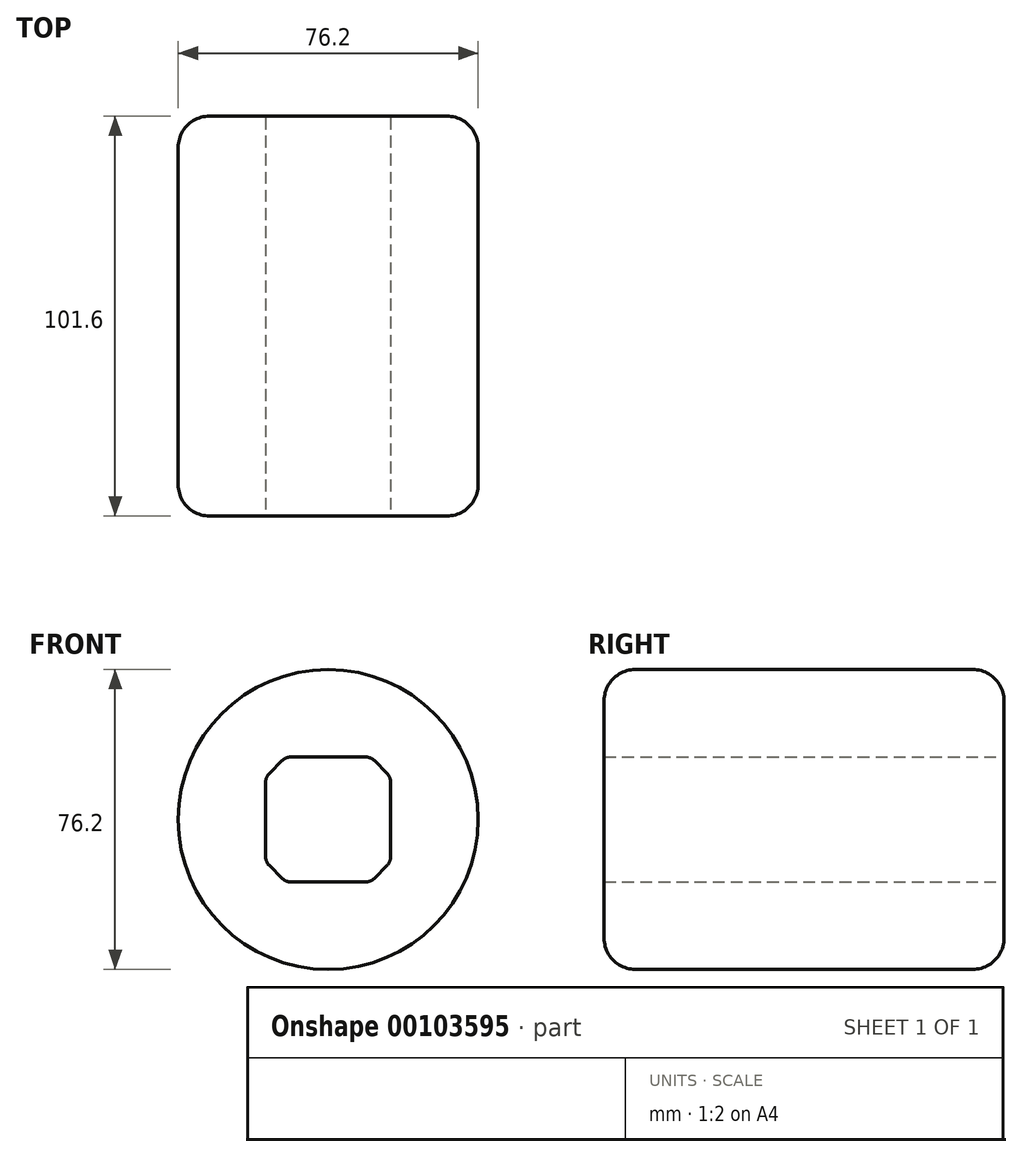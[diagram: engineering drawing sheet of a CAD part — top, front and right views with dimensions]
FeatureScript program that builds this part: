
annotation { "Feature Type Name" : "Feature", "Feature Type Description" : "" }
export const myFeature = defineFeature(function(context is Context, id is Id, definition is map)
    precondition{}
    {
        {
            var Q0;
            Q0=qCreatedBy(makeId("Front.planeOp"),FACE);
            var sketch = newSketch(context, id + "F0", { "sketchPlane" : qUnion([Q0])});
            skCircle(sketch, "E0", {"center": v(0, 0) * mm, "radius": 38.1 * mm});
            skSolve(sketch);
        }
        {
            var Q0;
            Q0 = qSketchRegion(id + "F0", true);
            extrude(context, id + "F1", {"entities" : qUnion([Q0]), "endBound" : BoundingType.SYMMETRIC, "depth" : 101.6 * mm});
        }
        {
            var Q0;
            Q0=makeQuery(id+"F1.opExtrude","CAP_EDGE",EDGE,{"disambiguationData":[OSD([sQuery(id+"F0.wireOp",EDGE,"E0")])],"isStart":false});
            var Q1;
            Q1=makeQuery(id+"F1.opExtrude","CAP_EDGE",EDGE,{"disambiguationData":[OSD([sQuery(id+"F0.wireOp",EDGE,"E0")])],"isStart":true});
            fillet(context, id + "F2", {"entities" : qUnion([Q0, Q1]), "radius" : 7.94 * mm, "tangentPropagation" : true, "allowEdgeOverflow" : false});
        }
        {
            var Q0;
            Q0=makeQuery(id+"F1.opExtrude","CAP_FACE",FACE,{"disambiguationData":[OSD([sQuery(id+"F0.wireOp",EDGE,"E0")])],"isStart":false});
            var sketch = newSketch(context, id + "F3", { "sketchPlane" : qUnion([Q0])});
            skLineSegment(sketch, "E1.bottom", {"start": v(15.88, -15.87) * mm, "end": v(-15.88, -15.88) * mm});
            skLineSegment(sketch, "E1.top", {"start": v(15.88, 15.88) * mm, "end": v(-15.88, 15.87) * mm});
            skLineSegment(sketch, "E1.left", {"start": v(15.88, -15.87) * mm, "end": v(15.88, 15.88) * mm});
            skLineSegment(sketch, "E1.right", {"start": v(-15.88, -15.88) * mm, "end": v(-15.88, 15.87) * mm});
            skPoint(sketch, "E1.middle", {"position": v(0, 0) * mm});
            skSolve(sketch);
        }
        {
            var Q0;
            Q0 = qSketchRegion(id + "F3", true);
            extrude(context, id + "F4", {"entities" : qUnion([Q0]), "operationType" : NewBodyOperationType.REMOVE, "endBound" : BoundingType.THROUGH_ALL, "oppositeDirection" : true, "depth" : 25.4 * mm});
        }
        {
            var Q0;
            Q0=makeQuery(id+"F4.boolean.opBoolean","COPY",EDGE,{"derivedFrom":makeQuery(id+"F4.opExtrude","SWEPT_EDGE",EDGE,{"disambiguationData":[OSD([sQuery(id+"F3.wireOp",EDGE,"E1.top"),sQuery(id+"F3.wireOp",EDGE,"E1.right")])]})});
            var Q1;
            Q1=makeQuery(id+"F4.boolean.opBoolean","COPY",EDGE,{"derivedFrom":makeQuery(id+"F4.opExtrude","SWEPT_EDGE",EDGE,{"disambiguationData":[OSD([sQuery(id+"F3.wireOp",EDGE,"E1.bottom"),sQuery(id+"F3.wireOp",EDGE,"E1.left")])]})});
            var Q2;
            Q2=makeQuery(id+"F4.boolean.opBoolean","COPY",EDGE,{"derivedFrom":makeQuery(id+"F4.opExtrude","SWEPT_EDGE",EDGE,{"disambiguationData":[OSD([sQuery(id+"F3.wireOp",EDGE,"E1.top"),sQuery(id+"F3.wireOp",EDGE,"E1.left")])]})});
            var Q3;
            Q3=makeQuery(id+"F4.boolean.opBoolean","COPY",EDGE,{"derivedFrom":makeQuery(id+"F4.opExtrude","SWEPT_EDGE",EDGE,{"disambiguationData":[OSD([sQuery(id+"F3.wireOp",EDGE,"E1.bottom"),sQuery(id+"F3.wireOp",EDGE,"E1.right")])]})});
            chamfer(context, id + "F5", {"entities" : qUnion([Q0, Q1, Q2, Q3]), "width" : 5.08 * mm, "tangentPropagation" : true});
        }
        {
            var Q0;
            {var subQ0=sQuery(id+"F3.wireOp",EDGE,"E1.bottom");Q0=makeQuery(id+"F5.opChamfer","BLEND_EDGE",EDGE,{"blendedFrom":[makeQuery(id+"F4.boolean.opBoolean","COPY",EDGE,{"derivedFrom":makeQuery(id+"F4.opExtrude","SWEPT_EDGE",EDGE,{"disambiguationData":[OSD([subQ0,sQuery(id+"F3.wireOp",EDGE,"E1.right")])]})}),makeQuery(id+"F4.boolean.opBoolean","COPY",FACE,{"derivedFrom":makeQuery(id+"F4.opExtrude","SWEPT_FACE",FACE,{"disambiguationData":[OSD([subQ0])]})})],"blendedInto":[makeQuery(id+"F4.boolean.opBoolean","COPY",FACE,{"derivedFrom":makeQuery(id+"F4.opExtrude","SWEPT_FACE",FACE,{"disambiguationData":[OSD([subQ0])]})})]});}
            var Q1;
            {var subQ0=sQuery(id+"F3.wireOp",EDGE,"E1.right");Q1=makeQuery(id+"F5.opChamfer","BLEND_EDGE",EDGE,{"blendedFrom":[makeQuery(id+"F4.boolean.opBoolean","COPY",EDGE,{"derivedFrom":makeQuery(id+"F4.opExtrude","SWEPT_EDGE",EDGE,{"disambiguationData":[OSD([sQuery(id+"F3.wireOp",EDGE,"E1.bottom"),subQ0])]})}),makeQuery(id+"F4.boolean.opBoolean","COPY",FACE,{"derivedFrom":makeQuery(id+"F4.opExtrude","SWEPT_FACE",FACE,{"disambiguationData":[OSD([subQ0])]})})],"blendedInto":[makeQuery(id+"F4.boolean.opBoolean","COPY",FACE,{"derivedFrom":makeQuery(id+"F4.opExtrude","SWEPT_FACE",FACE,{"disambiguationData":[OSD([subQ0])]})})]});}
            var Q2;
            {var subQ0=sQuery(id+"F3.wireOp",EDGE,"E1.right");Q2=makeQuery(id+"F5.opChamfer","BLEND_EDGE",EDGE,{"blendedFrom":[makeQuery(id+"F4.boolean.opBoolean","COPY",EDGE,{"derivedFrom":makeQuery(id+"F4.opExtrude","SWEPT_EDGE",EDGE,{"disambiguationData":[OSD([sQuery(id+"F3.wireOp",EDGE,"E1.top"),subQ0])]})}),makeQuery(id+"F4.boolean.opBoolean","COPY",FACE,{"derivedFrom":makeQuery(id+"F4.opExtrude","SWEPT_FACE",FACE,{"disambiguationData":[OSD([subQ0])]})})],"blendedInto":[makeQuery(id+"F4.boolean.opBoolean","COPY",FACE,{"derivedFrom":makeQuery(id+"F4.opExtrude","SWEPT_FACE",FACE,{"disambiguationData":[OSD([subQ0])]})})]});}
            var Q3;
            {var subQ0=sQuery(id+"F3.wireOp",EDGE,"E1.top");Q3=makeQuery(id+"F5.opChamfer","BLEND_EDGE",EDGE,{"blendedFrom":[makeQuery(id+"F4.boolean.opBoolean","COPY",EDGE,{"derivedFrom":makeQuery(id+"F4.opExtrude","SWEPT_EDGE",EDGE,{"disambiguationData":[OSD([subQ0,sQuery(id+"F3.wireOp",EDGE,"E1.right")])]})}),makeQuery(id+"F4.boolean.opBoolean","COPY",FACE,{"derivedFrom":makeQuery(id+"F4.opExtrude","SWEPT_FACE",FACE,{"disambiguationData":[OSD([subQ0])]})})],"blendedInto":[makeQuery(id+"F4.boolean.opBoolean","COPY",FACE,{"derivedFrom":makeQuery(id+"F4.opExtrude","SWEPT_FACE",FACE,{"disambiguationData":[OSD([subQ0])]})})]});}
            var Q4;
            {var subQ0=sQuery(id+"F3.wireOp",EDGE,"E1.top");Q4=makeQuery(id+"F5.opChamfer","BLEND_EDGE",EDGE,{"blendedFrom":[makeQuery(id+"F4.boolean.opBoolean","COPY",EDGE,{"derivedFrom":makeQuery(id+"F4.opExtrude","SWEPT_EDGE",EDGE,{"disambiguationData":[OSD([subQ0,sQuery(id+"F3.wireOp",EDGE,"E1.left")])]})}),makeQuery(id+"F4.boolean.opBoolean","COPY",FACE,{"derivedFrom":makeQuery(id+"F4.opExtrude","SWEPT_FACE",FACE,{"disambiguationData":[OSD([subQ0])]})})],"blendedInto":[makeQuery(id+"F4.boolean.opBoolean","COPY",FACE,{"derivedFrom":makeQuery(id+"F4.opExtrude","SWEPT_FACE",FACE,{"disambiguationData":[OSD([subQ0])]})})]});}
            var Q5;
            {var subQ0=sQuery(id+"F3.wireOp",EDGE,"E1.left");Q5=makeQuery(id+"F5.opChamfer","BLEND_EDGE",EDGE,{"blendedFrom":[makeQuery(id+"F4.boolean.opBoolean","COPY",EDGE,{"derivedFrom":makeQuery(id+"F4.opExtrude","SWEPT_EDGE",EDGE,{"disambiguationData":[OSD([sQuery(id+"F3.wireOp",EDGE,"E1.top"),subQ0])]})}),makeQuery(id+"F4.boolean.opBoolean","COPY",FACE,{"derivedFrom":makeQuery(id+"F4.opExtrude","SWEPT_FACE",FACE,{"disambiguationData":[OSD([subQ0])]})})],"blendedInto":[makeQuery(id+"F4.boolean.opBoolean","COPY",FACE,{"derivedFrom":makeQuery(id+"F4.opExtrude","SWEPT_FACE",FACE,{"disambiguationData":[OSD([subQ0])]})})]});}
            var Q6;
            {var subQ0=sQuery(id+"F3.wireOp",EDGE,"E1.left");Q6=makeQuery(id+"F5.opChamfer","BLEND_EDGE",EDGE,{"blendedFrom":[makeQuery(id+"F4.boolean.opBoolean","COPY",EDGE,{"derivedFrom":makeQuery(id+"F4.opExtrude","SWEPT_EDGE",EDGE,{"disambiguationData":[OSD([sQuery(id+"F3.wireOp",EDGE,"E1.bottom"),subQ0])]})}),makeQuery(id+"F4.boolean.opBoolean","COPY",FACE,{"derivedFrom":makeQuery(id+"F4.opExtrude","SWEPT_FACE",FACE,{"disambiguationData":[OSD([subQ0])]})})],"blendedInto":[makeQuery(id+"F4.boolean.opBoolean","COPY",FACE,{"derivedFrom":makeQuery(id+"F4.opExtrude","SWEPT_FACE",FACE,{"disambiguationData":[OSD([subQ0])]})})]});}
            var Q7;
            {var subQ0=sQuery(id+"F3.wireOp",EDGE,"E1.bottom");Q7=makeQuery(id+"F5.opChamfer","BLEND_EDGE",EDGE,{"blendedFrom":[makeQuery(id+"F4.boolean.opBoolean","COPY",EDGE,{"derivedFrom":makeQuery(id+"F4.opExtrude","SWEPT_EDGE",EDGE,{"disambiguationData":[OSD([subQ0,sQuery(id+"F3.wireOp",EDGE,"E1.left")])]})}),makeQuery(id+"F4.boolean.opBoolean","COPY",FACE,{"derivedFrom":makeQuery(id+"F4.opExtrude","SWEPT_FACE",FACE,{"disambiguationData":[OSD([subQ0])]})})],"blendedInto":[makeQuery(id+"F4.boolean.opBoolean","COPY",FACE,{"derivedFrom":makeQuery(id+"F4.opExtrude","SWEPT_FACE",FACE,{"disambiguationData":[OSD([subQ0])]})})]});}
            fillet(context, id + "F6", {"entities" : qUnion([Q0, Q1, Q2, Q3, Q4, Q5, Q6, Q7]), "radius" : 3.17 * mm, "tangentPropagation" : true, "allowEdgeOverflow" : false});
        }
        {
            var Q0;
            Q0=makeQuery(id+"F4.boolean.opBoolean","COPY",EDGE,{"derivedFrom":makeQuery(id+"F4.opExtrude","CAP_EDGE",EDGE,{"disambiguationData":[OSD([sQuery(id+"F3.wireOp",EDGE,"E1.top")])],"isStart":true})});
            var Q1;
            Q1=makeQuery(id+"F4.boolean.opBoolean","INTERSECT",EDGE,{"derivedFrom":[makeQuery(id+"F1.opExtrude","CAP_FACE",FACE,{"disambiguationData":[OSD([sQuery(id+"F0.wireOp",EDGE,"E0")])],"isStart":true}),makeQuery(id+"F4.opExtrude","SWEPT_FACE",FACE,{"disambiguationData":[OSD([sQuery(id+"F3.wireOp",EDGE,"E1.top")])]})]});
            fillet(context, id + "F7", {"entities" : qUnion([Q0, Q1]), "radius" : 0.38 * mm, "tangentPropagation" : true, "allowEdgeOverflow" : false});
        }
    });
